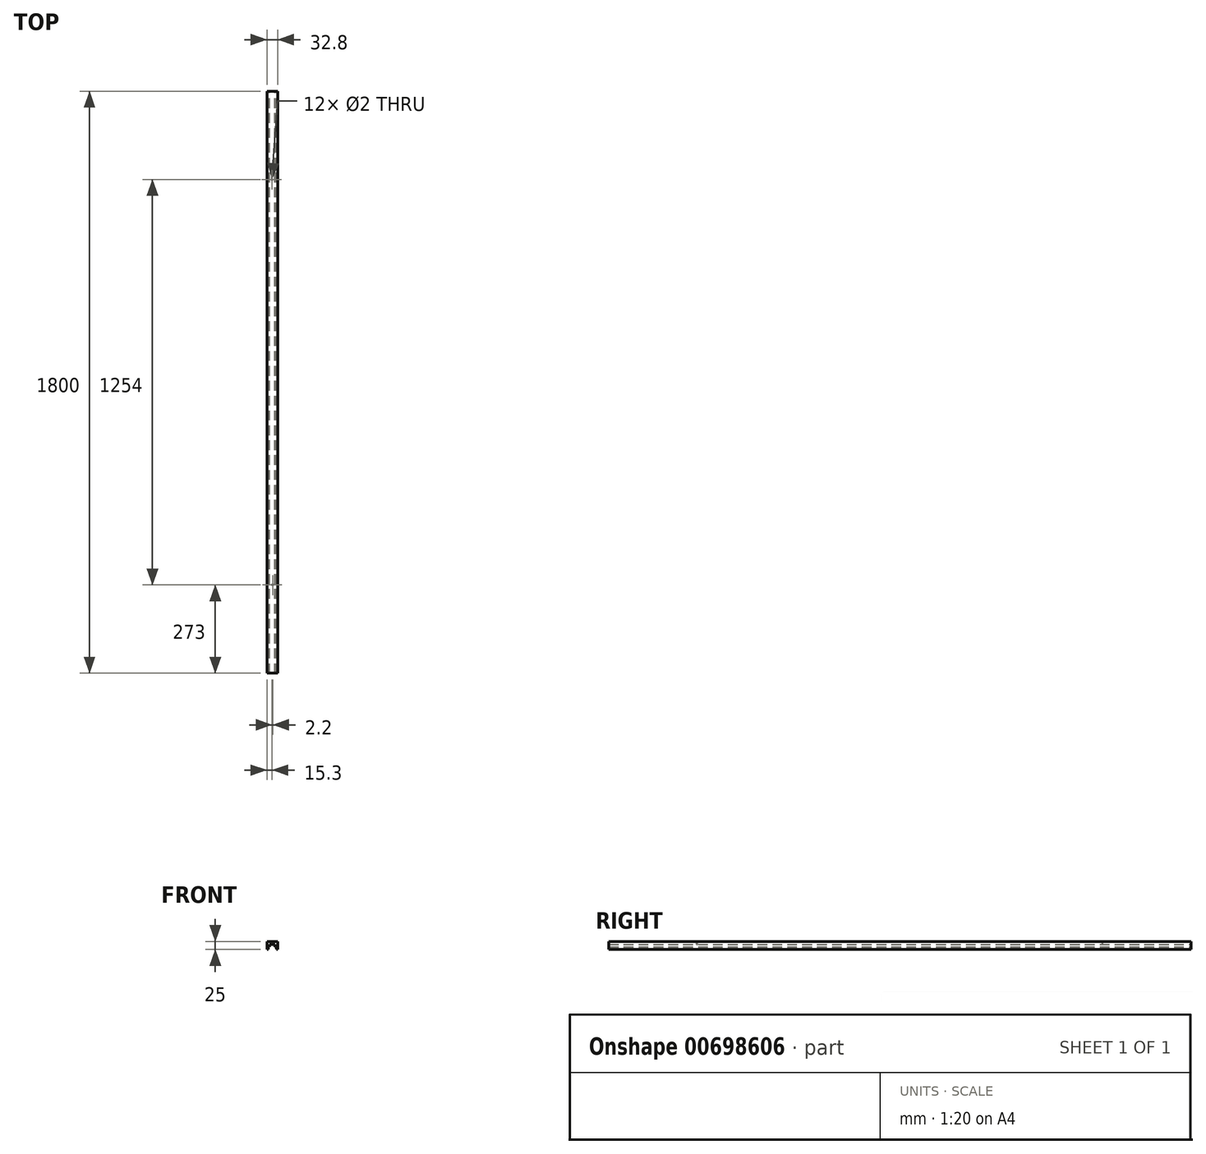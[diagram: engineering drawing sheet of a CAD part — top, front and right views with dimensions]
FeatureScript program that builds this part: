
annotation { "Feature Type Name" : "Feature", "Feature Type Description" : "" }
export const myFeature = defineFeature(function(context is Context, id is Id, definition is map)
    precondition{}
    {
        {
            var Q0;
            Q0=qCreatedBy(makeId("Front.planeOp"),FACE);
            var sketch = newSketch(context, id + "F0", { "sketchPlane" : qUnion([Q0])});
            skLineSegment(sketch, "E0.bottom", {"start": v(-16.35, 0.3) * mm, "end": v(16.45, 0.3) * mm});
            skLineSegment(sketch, "E0.right", {"start": v(16.45, 0.3) * mm, "end": v(16.45, 25.3) * mm});
            skLineSegment(sketch, "E1.bottom", {"start": v(16.45, 0.3) * mm, "end": v(12.55, 0.3) * mm});
            skLineSegment(sketch, "E1.top", {"start": v(16.45, 3.3) * mm, "end": v(12.55, 3.3) * mm});
            skLineSegment(sketch, "E1.left", {"start": v(16.45, 0.3) * mm, "end": v(16.45, 3.3) * mm});
            skLineSegment(sketch, "E1.right", {"start": v(12.55, 0.3) * mm, "end": v(12.55, 3.3) * mm});
            skLineSegment(sketch, "E2.bottom", {"start": v(12.55, 0.3) * mm, "end": v(-12.45, 0.3) * mm});
            skLineSegment(sketch, "E2.top", {"start": v(12.55, 3.3) * mm, "end": v(-12.45, 3.3) * mm});
            skLineSegment(sketch, "E2.right", {"start": v(-12.45, 0.3) * mm, "end": v(-12.45, 3.3) * mm});
            skLineSegment(sketch, "E3.bottom", {"start": v(-12.45, 3.3) * mm, "end": v(-8.35, 3.3) * mm});
            skLineSegment(sketch, "E3.top", {"start": v(-12.45, 8.47) * mm, "end": v(-8.35, 8.47) * mm});
            skLineSegment(sketch, "E3.left", {"start": v(-12.45, 3.3) * mm, "end": v(-12.45, 8.47) * mm});
            skLineSegment(sketch, "E3.right", {"start": v(-8.35, 3.3) * mm, "end": v(-8.35, 8.47) * mm});
            skLineSegment(sketch, "E4.bottom", {"start": v(12.55, 3.3) * mm, "end": v(8.45, 3.3) * mm});
            skLineSegment(sketch, "E4.top", {"start": v(12.55, 8.47) * mm, "end": v(8.45, 8.47) * mm});
            skLineSegment(sketch, "E4.left", {"start": v(12.55, 3.3) * mm, "end": v(12.55, 8.47) * mm});
            skLineSegment(sketch, "E4.right", {"start": v(8.45, 3.3) * mm, "end": v(8.45, 8.47) * mm});
            skLineSegment(sketch, "E5.bottom", {"start": v(-8.35, 3.3) * mm, "end": v(8.45, 3.3) * mm});
            skLineSegment(sketch, "E5.top", {"start": v(-8.35, 16.1) * mm, "end": v(8.45, 16.1) * mm});
            skLineSegment(sketch, "E5.left", {"start": v(-8.35, 3.3) * mm, "end": v(-8.35, 16.1) * mm});
            skLineSegment(sketch, "E5.right", {"start": v(8.45, 3.3) * mm, "end": v(8.45, 16.1) * mm});
            skPoint(sketch, "E6.top.end.orphan", {"position": v(-33.55, -309.7) * mm});
            skLineSegment(sketch, "E7.bottom", {"start": v(16.45, 0.3) * mm, "end": v(-12.45, 0.3) * mm});
            skLineSegment(sketch, "E7.right", {"start": v(-16.35, 0.3) * mm, "end": v(-16.35, 25.3) * mm});
            skPoint(sketch, "E8.orphan", {"position": v(-33.55, 0.3) * mm});
            skLineSegment(sketch, "E9.top", {"start": v(-16.35, 25.3) * mm, "end": v(16.45, 25.3) * mm});
            skPoint(sketch, "E7.top.start.orphan", {"position": v(16.45, 50.3) * mm});
            skSolve(sketch);
        }
        {
            var Q0;
            {var subQ0=sQuery(id+"F0.wireOp",EDGE,"E1.top");Q0=makeQuery(id+"F0.imprint","IMPRINT",FACE,{"disambiguationData":[TD([[makeQuery(id+"F0.imprint","IMPRINT",EDGE,{"derivedFrom":subQ0}),1.0]])]});}
            var Q1;
            {var subQ5=sQuery(id+"F0.wireOp",EDGE,"E1.top");Q1=makeQuery(id+"F0.imprint","IMPRINT",FACE,{"disambiguationData":[TD([[makeQuery(id+"F0.imprint","IMPRINT",EDGE,{"derivedFrom":subQ5}),-1.0]])]});}
            var Q2;
            {var subQ0=sQuery(id+"F0.wireOp",EDGE,"E3.bottom");Q2=makeQuery(id+"F0.imprint","IMPRINT",FACE,{"disambiguationData":[TD([[makeQuery(id+"F0.imprint","IMPRINT",EDGE,{"derivedFrom":subQ0}),1.0]])]});}
            var Q3;
            {var subQ0=sQuery(id+"F0.wireOp",EDGE,"E4.bottom");Q3=makeQuery(id+"F0.imprint","IMPRINT",FACE,{"disambiguationData":[TD([[makeQuery(id+"F0.imprint","IMPRINT",EDGE,{"derivedFrom":subQ0}),-1.0]])]});}
            extrude(context, id + "F1", {"entities" : qUnion([Q0, Q1, Q2, Q3]), "depth" : 2000 * mm, "offsetDistance" : 25 * mm});
        }
        {
            var Q0;
            Q0=makeQuery(id+"F1.opExtrude","SWEPT_FACE",FACE,{"disambiguationData":[OSD([sQuery(id+"F0.wireOp",EDGE,"E9.top")])]});
            var sketch = newSketch(context, id + "F2", { "sketchPlane" : qUnion([Q0])});
            skLineSegment(sketch, "E10.bottom", {"start": v(-16.35, 0) * mm, "end": v(1.15, -0.05) * mm, "construction": true});
            skLineSegment(sketch, "E11.bottom", {"start": v(-16.35, -2000) * mm, "end": v(1.15, -2000) * mm, "construction": true});
            skLineSegment(sketch, "E11.top", {"start": v(-16.35, -1627) * mm, "end": v(1.15, -1627) * mm, "construction": true});
            skLineSegment(sketch, "E11.left", {"start": v(-16.35, -2000) * mm, "end": v(-16.35, -1627) * mm, "construction": true});
            skLineSegment(sketch, "E11.right", {"start": v(1.15, -2000) * mm, "end": v(1.15, -1627) * mm, "construction": true});
            skPoint(sketch, "E12", {"position": v(1.15, -1627) * mm});
            skLineSegment(sketch, "E13.bottom", {"start": v(16.45, 0) * mm, "end": v(-1.05, 0) * mm, "construction": true});
            skLineSegment(sketch, "E13.top", {"start": v(16.45, -373) * mm, "end": v(-1.05, -373) * mm, "construction": true});
            skLineSegment(sketch, "E13.left", {"start": v(16.45, 0) * mm, "end": v(16.45, -373) * mm, "construction": true});
            skLineSegment(sketch, "E13.right", {"start": v(-1.05, 0) * mm, "end": v(-1.05, -373) * mm, "construction": true});
            skPoint(sketch, "E14", {"position": v(-1.05, -373) * mm});
            skSolve(sketch);
        }
        {
            var Q0;
            Q0=sQuery(id+"F2.wireOp",VERTEX,"E14");
            var Q1;
            Q1=sQuery(id+"F2.wireOp",VERTEX,"E12");
            var Q2;
            Q2=makeQuery(id+"F1.opExtrude","SWEPT_BODY",BODY,{"disambiguationData":[OSD([sQuery(id+"F0.wireOp",EDGE,"E1.right"),sQuery(id+"F0.wireOp",EDGE,"E2.right"),sQuery(id+"F0.wireOp",EDGE,"E3.bottom"),sQuery(id+"F0.wireOp",EDGE,"E4.bottom"),sQuery(id+"F0.wireOp",EDGE,"E5.top"),sQuery(id+"F0.wireOp",EDGE,"E5.left"),sQuery(id+"F0.wireOp",EDGE,"E5.right"),sQuery(id+"F0.wireOp",EDGE,"E0.bottom"),sQuery(id+"F0.wireOp",EDGE,"E9.top"),sQuery(id+"F0.wireOp",EDGE,"E7.right"),sQuery(id+"F0.wireOp",EDGE,"E0.right")])]});
            hole(context, id + "F3", {"style" : HoleStyle.SIMPLE, "endStyle" : HoleEndStyle.THROUGH, "holeDiameter" : 2 * mm, "majorDiameter" : 5 * mm, "isTappedThrough" : true, "tappedDepth" : 12 * mm, "tapClearance" : 3, "startFromSketch" : true, "locations" : qUnion([Q0, Q1]), "scope" : qUnion([Q2])});
        }
        {
            var Q0;
            Q0=makeQuery(id+"F1.opExtrude","SWEPT_FACE",FACE,{"disambiguationData":[OSD([sQuery(id+"F0.wireOp",EDGE,"E9.top")])]});
            var sketch = newSketch(context, id + "F4", { "sketchPlane" : qUnion([Q0])});
            skLineSegment(sketch, "E15.bottom", {"start": v(-16.35, -2000) * mm, "end": v(16.45, -2000) * mm});
            skLineSegment(sketch, "E15.top", {"start": v(-16.35, -1900) * mm, "end": v(16.45, -1900) * mm});
            skLineSegment(sketch, "E15.left", {"start": v(-16.35, -2000) * mm, "end": v(-16.35, -1900) * mm});
            skLineSegment(sketch, "E15.right", {"start": v(16.45, -2000) * mm, "end": v(16.45, -1900) * mm});
            skLineSegment(sketch, "E16.bottom", {"start": v(-16.35, 0) * mm, "end": v(16.45, 0) * mm});
            skLineSegment(sketch, "E16.top", {"start": v(-16.35, -100) * mm, "end": v(16.45, -100) * mm});
            skLineSegment(sketch, "E16.left", {"start": v(-16.35, 0) * mm, "end": v(-16.35, -100) * mm});
            skLineSegment(sketch, "E16.right", {"start": v(16.45, 0) * mm, "end": v(16.45, -100) * mm});
            skSolve(sketch);
        }
        {
            var Q0;
            Q0=makeQuery(id+"F4.imprint","IMPRINT",FACE,{"disambiguationData":[TD([[makeQuery(id+"F4.imprint","IMPRINT",EDGE,{"derivedFrom":sQuery(id+"F4.wireOp",EDGE,"E16.bottom")}),-1.0]])]});
            var Q1;
            Q1=makeQuery(id+"F4.imprint","IMPRINT",FACE,{"disambiguationData":[TD([[makeQuery(id+"F4.imprint","IMPRINT",EDGE,{"derivedFrom":sQuery(id+"F4.wireOp",EDGE,"E15.bottom")}),1.0]])]});
            extrude(context, id + "F5", {"entities" : qUnion([Q0, Q1]), "operationType" : NewBodyOperationType.REMOVE, "endBound" : BoundingType.THROUGH_ALL, "oppositeDirection" : true, "depth" : 25 * mm, "offsetDistance" : 25 * mm});
        }
    });
